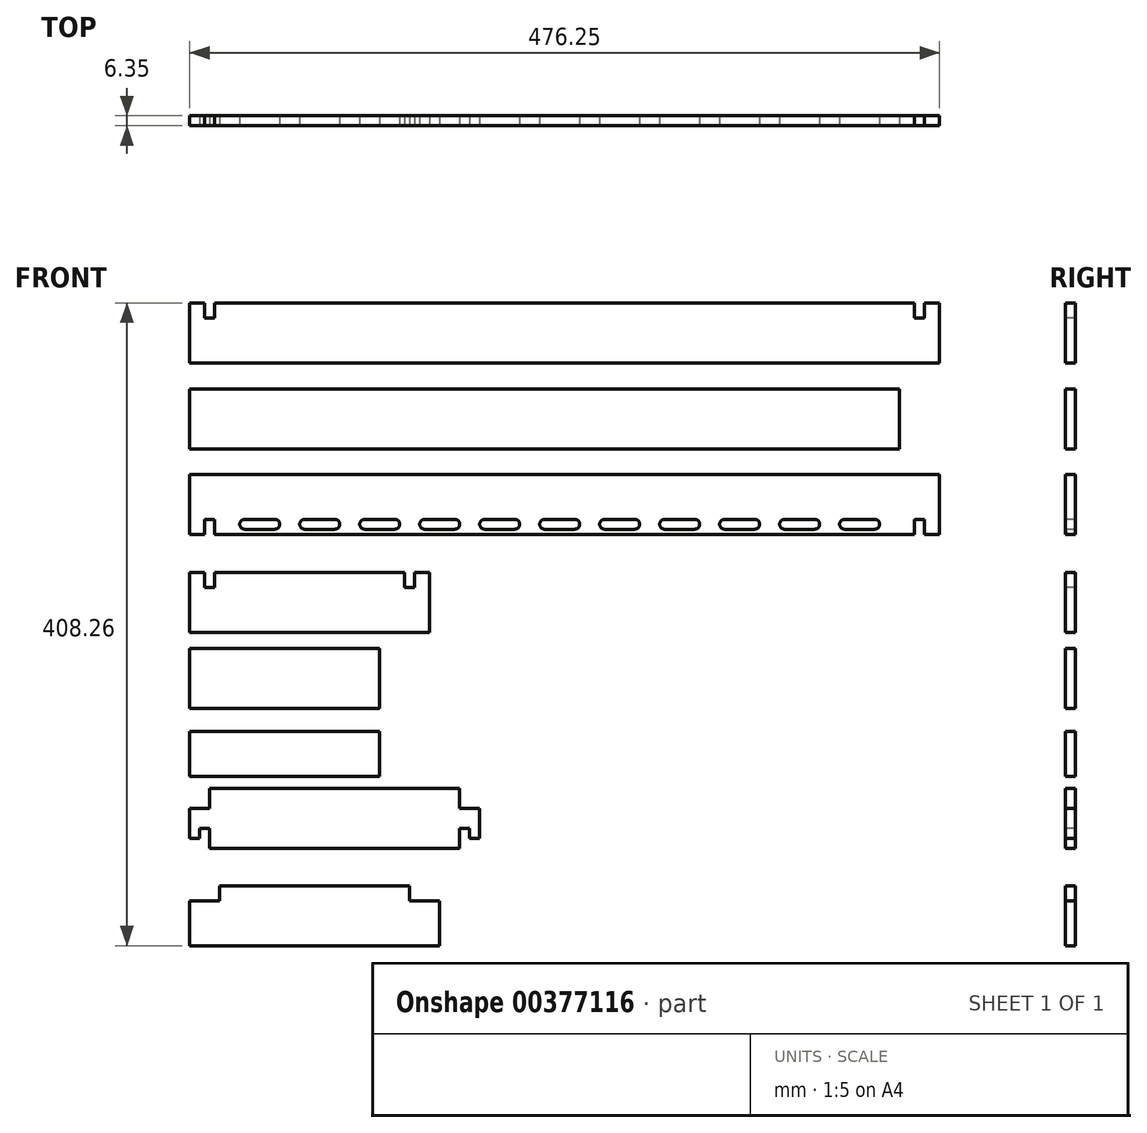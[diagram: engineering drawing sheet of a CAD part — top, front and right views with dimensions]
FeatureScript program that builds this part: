
annotation { "Feature Type Name" : "Feature", "Feature Type Description" : "" }
export const myFeature = defineFeature(function(context is Context, id is Id, definition is map)
    precondition{}
    {
        {
            var Q0;
            Q0=qCreatedBy(makeId("Front.planeOp"),FACE);
            var sketch = newSketch(context, id + "F0", { "sketchPlane" : qUnion([Q0])});
            skLineSegment(sketch, "E0.bottom", {"start": v(0, 0) * mm, "end": v(476.25, 0) * mm});
            skLineSegment(sketch, "E0.top", {"start": v(0, 38.1) * mm, "end": v(476.25, 38.1) * mm});
            skLineSegment(sketch, "E0.left", {"start": v(0, 0) * mm, "end": v(0, 38.1) * mm});
            skLineSegment(sketch, "E0.right", {"start": v(476.25, 0) * mm, "end": v(476.25, 38.1) * mm});
            skSolve(sketch);
        }
        {
            var Q0;
            Q0=qCreatedBy(makeId("Front.planeOp"),FACE);
            var sketch = newSketch(context, id + "F1", { "sketchPlane" : qUnion([Q0])});
            skLineSegment(sketch, "E1.bottom", {"start": v(0, -133.14) * mm, "end": v(152.4, -133.14) * mm});
            skLineSegment(sketch, "E1.top", {"start": v(0, -171.24) * mm, "end": v(152.4, -171.24) * mm});
            skLineSegment(sketch, "E1.left", {"start": v(0, -133.14) * mm, "end": v(0, -171.24) * mm});
            skLineSegment(sketch, "E1.right", {"start": v(152.4, -133.14) * mm, "end": v(152.4, -171.24) * mm});
            skLineSegment(sketch, "E2.bottom", {"start": v(0, -181.45) * mm, "end": v(120.65, -181.45) * mm});
            skLineSegment(sketch, "E2.top", {"start": v(0, -219.55) * mm, "end": v(120.65, -219.55) * mm});
            skLineSegment(sketch, "E2.left", {"start": v(0, -181.45) * mm, "end": v(0, -219.55) * mm});
            skLineSegment(sketch, "E2.right", {"start": v(120.65, -181.45) * mm, "end": v(120.65, -219.55) * mm});
            skLineSegment(sketch, "E3.bottom", {"start": v(0, -234.04) * mm, "end": v(120.65, -234.04) * mm});
            skLineSegment(sketch, "E3.top", {"start": v(0, -262.61) * mm, "end": v(120.65, -262.61) * mm});
            skLineSegment(sketch, "E3.left", {"start": v(0, -234.04) * mm, "end": v(0, -262.61) * mm});
            skLineSegment(sketch, "E3.right", {"start": v(120.65, -234.04) * mm, "end": v(120.65, -262.61) * mm});
            skLineSegment(sketch, "E4.bottom", {"start": v(0, -270.37) * mm, "end": v(184.15, -270.37) * mm});
            skLineSegment(sketch, "E4.top", {"start": v(0, -308.47) * mm, "end": v(184.15, -308.47) * mm});
            skLineSegment(sketch, "E4.left", {"start": v(0, -270.37) * mm, "end": v(0, -308.47) * mm});
            skLineSegment(sketch, "E4.right", {"start": v(184.15, -270.37) * mm, "end": v(184.15, -308.47) * mm});
            skLineSegment(sketch, "E5.bottom", {"start": v(0, -332.06) * mm, "end": v(158.75, -332.06) * mm});
            skLineSegment(sketch, "E5.top", {"start": v(0, -370.16) * mm, "end": v(158.75, -370.16) * mm});
            skLineSegment(sketch, "E5.left", {"start": v(0, -332.06) * mm, "end": v(0, -370.16) * mm});
            skLineSegment(sketch, "E5.right", {"start": v(158.75, -332.06) * mm, "end": v(158.75, -370.16) * mm});
            skSolve(sketch);
        }
        {
            var Q0;
            Q0=makeQuery(id+"F0.imprint","IMPRINT",FACE,{"disambiguationData":[TD([[makeQuery(id+"F0.imprint","IMPRINT",EDGE,{"derivedFrom":sQuery(id+"F0.wireOp",EDGE,"E0.bottom")}),1.0]])]});
            var Q1;
            Q1=makeQuery(id+"F1.imprint","IMPRINT",FACE,{"disambiguationData":[TD([[makeQuery(id+"F1.imprint","IMPRINT",EDGE,{"derivedFrom":sQuery(id+"F1.wireOp",EDGE,"E1.bottom")}),-1.0]])]});
            var Q2;
            Q2=makeQuery(id+"F1.imprint","IMPRINT",FACE,{"disambiguationData":[TD([[makeQuery(id+"F1.imprint","IMPRINT",EDGE,{"derivedFrom":sQuery(id+"F1.wireOp",EDGE,"E2.bottom")}),-1.0]])]});
            var Q3;
            Q3=makeQuery(id+"F1.imprint","IMPRINT",FACE,{"disambiguationData":[TD([[makeQuery(id+"F1.imprint","IMPRINT",EDGE,{"derivedFrom":sQuery(id+"F1.wireOp",EDGE,"E3.bottom")}),-1.0]])]});
            var Q4;
            Q4=makeQuery(id+"F1.imprint","IMPRINT",FACE,{"disambiguationData":[TD([[makeQuery(id+"F1.imprint","IMPRINT",EDGE,{"derivedFrom":sQuery(id+"F1.wireOp",EDGE,"E4.bottom")}),-1.0]])]});
            var Q5;
            Q5=makeQuery(id+"F1.imprint","IMPRINT",FACE,{"disambiguationData":[TD([[makeQuery(id+"F1.imprint","IMPRINT",EDGE,{"derivedFrom":sQuery(id+"F1.wireOp",EDGE,"E5.bottom")}),-1.0]])]});
            extrude(context, id + "F2", {"entities" : qUnion([Q0, Q1, Q2, Q3, Q4, Q5]), "oppositeDirection" : true, "depth" : 6.35 * mm});
        }
        {
            var Q0;
            Q0=qCreatedBy(makeId("Front.planeOp"),FACE);
            var sketch = newSketch(context, id + "F3", { "sketchPlane" : qUnion([Q0])});
            skLineSegment(sketch, "E6.bottom", {"start": v(0, -70.73) * mm, "end": v(476.25, -70.73) * mm});
            skLineSegment(sketch, "E6.top", {"start": v(0, -108.83) * mm, "end": v(476.25, -108.83) * mm});
            skLineSegment(sketch, "E6.left", {"start": v(0, -70.73) * mm, "end": v(0, -108.83) * mm});
            skLineSegment(sketch, "E6.right", {"start": v(476.25, -70.73) * mm, "end": v(476.25, -108.83) * mm});
            skSolve(sketch);
        }
        {
            var Q0;
            Q0 = qSketchRegion(id + "F3", true);
            extrude(context, id + "F4", {"entities" : qUnion([Q0]), "oppositeDirection" : true, "depth" : 6.35 * mm});
        }
        {
            var Q0;
            Q0=qCreatedBy(makeId("Front.planeOp"),FACE);
            var sketch = newSketch(context, id + "F5", { "sketchPlane" : qUnion([Q0])});
            skLineSegment(sketch, "E7.bottom", {"start": v(9.52, 38.1) * mm, "end": v(15.88, 38.1) * mm});
            skLineSegment(sketch, "E7.top", {"start": v(9.53, 28.58) * mm, "end": v(15.87, 28.58) * mm});
            skLineSegment(sketch, "E7.left", {"start": v(9.52, 38.1) * mm, "end": v(9.53, 28.58) * mm});
            skLineSegment(sketch, "E7.right", {"start": v(15.88, 38.1) * mm, "end": v(15.88, 28.58) * mm});
            skLineSegment(sketch, "E8.bottom", {"start": v(460.38, 38.1) * mm, "end": v(466.73, 38.1) * mm});
            skLineSegment(sketch, "E8.top", {"start": v(460.38, 28.58) * mm, "end": v(466.73, 28.58) * mm});
            skLineSegment(sketch, "E8.left", {"start": v(460.38, 38.1) * mm, "end": v(460.38, 28.58) * mm});
            skLineSegment(sketch, "E8.right", {"start": v(466.73, 38.1) * mm, "end": v(466.73, 28.58) * mm});
            skLineSegment(sketch, "E9.bottom", {"start": v(9.53, -108.83) * mm, "end": v(15.87, -108.83) * mm});
            skLineSegment(sketch, "E9.top", {"start": v(9.52, -99.3) * mm, "end": v(15.87, -99.3) * mm});
            skLineSegment(sketch, "E9.left", {"start": v(9.53, -108.83) * mm, "end": v(9.52, -99.3) * mm});
            skLineSegment(sketch, "E9.right", {"start": v(15.87, -108.83) * mm, "end": v(15.87, -99.3) * mm});
            skLineSegment(sketch, "E10.bottom", {"start": v(460.38, -99.3) * mm, "end": v(466.73, -99.3) * mm});
            skLineSegment(sketch, "E10.top", {"start": v(460.38, -108.83) * mm, "end": v(466.73, -108.83) * mm});
            skLineSegment(sketch, "E10.left", {"start": v(460.38, -99.3) * mm, "end": v(460.38, -108.83) * mm});
            skLineSegment(sketch, "E10.right", {"start": v(466.73, -99.3) * mm, "end": v(466.73, -108.83) * mm});
            skLineSegment(sketch, "E11.bottom", {"start": v(9.53, -133.14) * mm, "end": v(15.87, -133.14) * mm});
            skLineSegment(sketch, "E11.top", {"start": v(9.53, -142.66) * mm, "end": v(15.87, -142.66) * mm});
            skLineSegment(sketch, "E11.left", {"start": v(9.53, -133.14) * mm, "end": v(9.53, -142.66) * mm});
            skLineSegment(sketch, "E11.right", {"start": v(15.87, -133.14) * mm, "end": v(15.87, -142.66) * mm});
            skLineSegment(sketch, "E12.bottom", {"start": v(136.53, -142.66) * mm, "end": v(142.88, -142.66) * mm});
            skLineSegment(sketch, "E12.top", {"start": v(136.53, -133.14) * mm, "end": v(142.88, -133.14) * mm});
            skLineSegment(sketch, "E12.left", {"start": v(136.53, -142.66) * mm, "end": v(136.53, -133.14) * mm});
            skLineSegment(sketch, "E12.right", {"start": v(142.88, -142.66) * mm, "end": v(142.88, -133.14) * mm});
            skLineSegment(sketch, "E13.bottom", {"start": v(34.93, -99.3) * mm, "end": v(53.98, -99.3) * mm});
            skLineSegment(sketch, "E13.top", {"start": v(34.93, -105.66) * mm, "end": v(53.98, -105.66) * mm});
            skLineSegment(sketch, "E13.left", {"start": v(31.75, -102.48) * mm, "end": v(31.75, -102.48) * mm});
            skLineSegment(sketch, "E13.right", {"start": v(57.15, -102.48) * mm, "end": v(57.15, -102.48) * mm});
            skPoint(sketch, "E14.visualSharp", {"position": v(31.75, -99.3) * mm});
            skArc(sketch, "E14.filletArc", {"start": v(34.93, -99.3) * mm, "mid": v(32.68, -100.24) * mm, "end": v(31.75, -102.48) * mm});
            skPoint(sketch, "E15.visualSharp", {"position": v(31.75, -105.66) * mm});
            skArc(sketch, "E15.filletArc", {"start": v(31.75, -102.48) * mm, "mid": v(32.68, -104.73) * mm, "end": v(34.93, -105.66) * mm});
            skPoint(sketch, "E16.visualSharp", {"position": v(57.15, -105.66) * mm});
            skArc(sketch, "E16.filletArc", {"start": v(53.98, -105.66) * mm, "mid": v(56.22, -104.73) * mm, "end": v(57.15, -102.48) * mm});
            skPoint(sketch, "E17.visualSharp", {"position": v(57.15, -99.3) * mm});
            skArc(sketch, "E17.filletArc", {"start": v(57.15, -102.48) * mm, "mid": v(56.22, -100.24) * mm, "end": v(53.98, -99.3) * mm});
            skArc(sketch, "E18.1.0.0", {"start": v(73.02, -99.3) * mm, "mid": v(70.78, -100.24) * mm, "end": v(69.85, -102.48) * mm});
            skArc(sketch, "E18.1.0.1", {"start": v(69.85, -102.48) * mm, "mid": v(70.78, -104.73) * mm, "end": v(73.02, -105.66) * mm});
            skLineSegment(sketch, "E18.1.0.2", {"start": v(73.02, -105.66) * mm, "end": v(92.07, -105.66) * mm});
            skArc(sketch, "E18.1.0.3", {"start": v(92.07, -105.66) * mm, "mid": v(94.32, -104.73) * mm, "end": v(95.25, -102.48) * mm});
            skArc(sketch, "E18.1.0.4", {"start": v(95.25, -102.48) * mm, "mid": v(94.32, -100.24) * mm, "end": v(92.07, -99.3) * mm});
            skLineSegment(sketch, "E18.1.0.5", {"start": v(73.02, -99.3) * mm, "end": v(92.07, -99.3) * mm});
            skArc(sketch, "E18.2.0.0", {"start": v(111.12, -99.3) * mm, "mid": v(108.88, -100.24) * mm, "end": v(107.95, -102.48) * mm});
            skArc(sketch, "E18.2.0.1", {"start": v(107.95, -102.48) * mm, "mid": v(108.88, -104.73) * mm, "end": v(111.12, -105.66) * mm});
            skLineSegment(sketch, "E18.2.0.2", {"start": v(111.12, -105.66) * mm, "end": v(130.17, -105.66) * mm});
            skArc(sketch, "E18.2.0.3", {"start": v(130.17, -105.66) * mm, "mid": v(132.42, -104.73) * mm, "end": v(133.35, -102.48) * mm});
            skArc(sketch, "E18.2.0.4", {"start": v(133.35, -102.48) * mm, "mid": v(132.42, -100.24) * mm, "end": v(130.17, -99.3) * mm});
            skLineSegment(sketch, "E18.2.0.5", {"start": v(111.12, -99.3) * mm, "end": v(130.17, -99.3) * mm});
            skLineSegment(sketch, "E18.direction1", {"start": v(31.75, -102.48) * mm, "end": v(69.85, -102.48) * mm, "construction": true});
            skArc(sketch, "E19.0.3.0", {"start": v(149.22, -99.3) * mm, "mid": v(146.98, -100.24) * mm, "end": v(146.05, -102.48) * mm});
            skArc(sketch, "E19.4.3.0", {"start": v(146.05, -102.48) * mm, "mid": v(146.98, -104.73) * mm, "end": v(149.22, -105.66) * mm});
            skLineSegment(sketch, "E19.8.3.0", {"start": v(149.22, -105.66) * mm, "end": v(168.27, -105.66) * mm});
            skArc(sketch, "E19.11.3.0", {"start": v(168.27, -105.66) * mm, "mid": v(170.52, -104.73) * mm, "end": v(171.45, -102.48) * mm});
            skArc(sketch, "E19.15.3.0", {"start": v(171.45, -102.48) * mm, "mid": v(170.52, -100.24) * mm, "end": v(168.27, -99.3) * mm});
            skLineSegment(sketch, "E19.19.3.0", {"start": v(149.22, -99.3) * mm, "end": v(168.27, -99.3) * mm});
            skArc(sketch, "E19.0.4.0", {"start": v(187.32, -99.3) * mm, "mid": v(185.08, -100.24) * mm, "end": v(184.15, -102.48) * mm});
            skArc(sketch, "E19.4.4.0", {"start": v(184.15, -102.48) * mm, "mid": v(185.08, -104.73) * mm, "end": v(187.32, -105.66) * mm});
            skLineSegment(sketch, "E19.8.4.0", {"start": v(187.32, -105.66) * mm, "end": v(206.37, -105.66) * mm});
            skArc(sketch, "E19.11.4.0", {"start": v(206.37, -105.66) * mm, "mid": v(208.62, -104.73) * mm, "end": v(209.55, -102.48) * mm});
            skArc(sketch, "E19.15.4.0", {"start": v(209.55, -102.48) * mm, "mid": v(208.62, -100.24) * mm, "end": v(206.37, -99.3) * mm});
            skLineSegment(sketch, "E19.19.4.0", {"start": v(187.32, -99.3) * mm, "end": v(206.37, -99.3) * mm});
            skArc(sketch, "E20.0.5.0", {"start": v(225.42, -99.3) * mm, "mid": v(223.18, -100.24) * mm, "end": v(222.25, -102.48) * mm});
            skArc(sketch, "E20.4.5.0", {"start": v(222.25, -102.48) * mm, "mid": v(223.18, -104.73) * mm, "end": v(225.42, -105.66) * mm});
            skLineSegment(sketch, "E20.8.5.0", {"start": v(225.42, -105.66) * mm, "end": v(244.47, -105.66) * mm});
            skArc(sketch, "E20.11.5.0", {"start": v(244.47, -105.66) * mm, "mid": v(246.72, -104.73) * mm, "end": v(247.65, -102.48) * mm});
            skArc(sketch, "E20.15.5.0", {"start": v(247.65, -102.48) * mm, "mid": v(246.72, -100.24) * mm, "end": v(244.47, -99.3) * mm});
            skLineSegment(sketch, "E20.19.5.0", {"start": v(225.42, -99.3) * mm, "end": v(244.47, -99.3) * mm});
            skArc(sketch, "E20.0.6.0", {"start": v(263.52, -99.3) * mm, "mid": v(261.28, -100.24) * mm, "end": v(260.35, -102.48) * mm});
            skArc(sketch, "E20.4.6.0", {"start": v(260.35, -102.48) * mm, "mid": v(261.28, -104.73) * mm, "end": v(263.52, -105.66) * mm});
            skLineSegment(sketch, "E20.8.6.0", {"start": v(263.52, -105.66) * mm, "end": v(282.57, -105.66) * mm});
            skArc(sketch, "E20.11.6.0", {"start": v(282.57, -105.66) * mm, "mid": v(284.82, -104.73) * mm, "end": v(285.75, -102.48) * mm});
            skArc(sketch, "E20.15.6.0", {"start": v(285.75, -102.48) * mm, "mid": v(284.82, -100.24) * mm, "end": v(282.57, -99.3) * mm});
            skLineSegment(sketch, "E20.19.6.0", {"start": v(263.52, -99.3) * mm, "end": v(282.57, -99.3) * mm});
            skArc(sketch, "E20.0.7.0", {"start": v(301.62, -99.3) * mm, "mid": v(299.38, -100.24) * mm, "end": v(298.45, -102.48) * mm});
            skArc(sketch, "E20.4.7.0", {"start": v(298.45, -102.48) * mm, "mid": v(299.38, -104.73) * mm, "end": v(301.62, -105.66) * mm});
            skLineSegment(sketch, "E20.8.7.0", {"start": v(301.62, -105.66) * mm, "end": v(320.67, -105.66) * mm});
            skArc(sketch, "E20.11.7.0", {"start": v(320.67, -105.66) * mm, "mid": v(322.92, -104.73) * mm, "end": v(323.85, -102.48) * mm});
            skArc(sketch, "E20.15.7.0", {"start": v(323.85, -102.48) * mm, "mid": v(322.92, -100.24) * mm, "end": v(320.67, -99.3) * mm});
            skLineSegment(sketch, "E20.19.7.0", {"start": v(301.62, -99.3) * mm, "end": v(320.67, -99.3) * mm});
            skArc(sketch, "E20.0.8.0", {"start": v(339.72, -99.3) * mm, "mid": v(337.48, -100.24) * mm, "end": v(336.55, -102.48) * mm});
            skArc(sketch, "E20.4.8.0", {"start": v(336.55, -102.48) * mm, "mid": v(337.48, -104.73) * mm, "end": v(339.72, -105.66) * mm});
            skLineSegment(sketch, "E20.8.8.0", {"start": v(339.72, -105.66) * mm, "end": v(358.77, -105.66) * mm});
            skArc(sketch, "E20.11.8.0", {"start": v(358.77, -105.66) * mm, "mid": v(361.02, -104.73) * mm, "end": v(361.95, -102.48) * mm});
            skArc(sketch, "E20.15.8.0", {"start": v(361.95, -102.48) * mm, "mid": v(361.02, -100.24) * mm, "end": v(358.77, -99.3) * mm});
            skLineSegment(sketch, "E20.19.8.0", {"start": v(339.72, -99.3) * mm, "end": v(358.77, -99.3) * mm});
            skArc(sketch, "E20.0.9.0", {"start": v(377.82, -99.3) * mm, "mid": v(375.58, -100.24) * mm, "end": v(374.65, -102.48) * mm});
            skArc(sketch, "E20.4.9.0", {"start": v(374.65, -102.48) * mm, "mid": v(375.58, -104.73) * mm, "end": v(377.82, -105.66) * mm});
            skLineSegment(sketch, "E20.8.9.0", {"start": v(377.82, -105.66) * mm, "end": v(396.87, -105.66) * mm});
            skArc(sketch, "E20.11.9.0", {"start": v(396.87, -105.66) * mm, "mid": v(399.12, -104.73) * mm, "end": v(400.05, -102.48) * mm});
            skArc(sketch, "E20.15.9.0", {"start": v(400.05, -102.48) * mm, "mid": v(399.12, -100.24) * mm, "end": v(396.87, -99.3) * mm});
            skLineSegment(sketch, "E20.19.9.0", {"start": v(377.82, -99.3) * mm, "end": v(396.87, -99.3) * mm});
            skLineSegment(sketch, "E21.bottom", {"start": v(0, -270.37) * mm, "end": v(12.7, -270.37) * mm});
            skLineSegment(sketch, "E21.top", {"start": v(0, -283.07) * mm, "end": v(12.7, -283.07) * mm});
            skLineSegment(sketch, "E21.left", {"start": v(0, -270.37) * mm, "end": v(0, -283.07) * mm});
            skLineSegment(sketch, "E21.right", {"start": v(12.7, -270.37) * mm, "end": v(12.7, -283.07) * mm});
            skLineSegment(sketch, "E22.bottom", {"start": v(184.15, -270.37) * mm, "end": v(171.45, -270.37) * mm});
            skLineSegment(sketch, "E22.top", {"start": v(184.15, -283.07) * mm, "end": v(171.45, -283.07) * mm});
            skLineSegment(sketch, "E22.left", {"start": v(184.15, -270.37) * mm, "end": v(184.15, -283.07) * mm});
            skLineSegment(sketch, "E22.right", {"start": v(171.45, -270.37) * mm, "end": v(171.45, -283.07) * mm});
            skLineSegment(sketch, "E23.bottom", {"start": v(171.45, -295.77) * mm, "end": v(177.8, -295.77) * mm});
            skLineSegment(sketch, "E23.left", {"start": v(171.45, -295.77) * mm, "end": v(171.45, -308.47) * mm});
            skLineSegment(sketch, "E24.bottom", {"start": v(6.35, -295.77) * mm, "end": v(12.7, -295.77) * mm});
            skLineSegment(sketch, "E24.top", {"start": v(0, -308.47) * mm, "end": v(12.7, -308.47) * mm});
            skLineSegment(sketch, "E24.right", {"start": v(12.7, -295.77) * mm, "end": v(12.7, -308.47) * mm});
            skLineSegment(sketch, "E25", {"start": v(0, -308.47) * mm, "end": v(0, -302.12) * mm});
            skLineSegment(sketch, "E26", {"start": v(0, -302.12) * mm, "end": v(6.35, -302.12) * mm});
            skLineSegment(sketch, "E27", {"start": v(6.35, -302.12) * mm, "end": v(6.35, -295.77) * mm});
            skLineSegment(sketch, "E28", {"start": v(177.8, -295.77) * mm, "end": v(177.8, -302.12) * mm});
            skLineSegment(sketch, "E29", {"start": v(177.8, -302.12) * mm, "end": v(184.15, -302.12) * mm});
            skLineSegment(sketch, "E30", {"start": v(184.15, -302.12) * mm, "end": v(184.15, -308.47) * mm});
            skLineSegment(sketch, "E31", {"start": v(171.45, -308.47) * mm, "end": v(184.15, -308.47) * mm});
            skLineSegment(sketch, "E32.bottom", {"start": v(0, -332.06) * mm, "end": v(19.05, -332.06) * mm});
            skLineSegment(sketch, "E32.top", {"start": v(0, -341.59) * mm, "end": v(19.05, -341.59) * mm});
            skLineSegment(sketch, "E32.left", {"start": v(0, -332.06) * mm, "end": v(0, -341.59) * mm});
            skLineSegment(sketch, "E32.right", {"start": v(19.05, -332.06) * mm, "end": v(19.05, -341.59) * mm});
            skLineSegment(sketch, "E33.bottom", {"start": v(139.7, -332.06) * mm, "end": v(158.75, -332.06) * mm});
            skLineSegment(sketch, "E33.top", {"start": v(139.7, -341.59) * mm, "end": v(158.75, -341.59) * mm});
            skLineSegment(sketch, "E33.left", {"start": v(139.7, -332.06) * mm, "end": v(139.7, -341.59) * mm});
            skLineSegment(sketch, "E33.right", {"start": v(158.75, -332.06) * mm, "end": v(158.75, -341.59) * mm});
            skArc(sketch, "E34.0.10.0", {"start": v(415.92, -99.3) * mm, "mid": v(413.68, -100.24) * mm, "end": v(412.75, -102.48) * mm});
            skArc(sketch, "E34.4.10.0", {"start": v(412.75, -102.48) * mm, "mid": v(413.68, -104.73) * mm, "end": v(415.92, -105.66) * mm});
            skLineSegment(sketch, "E34.8.10.0", {"start": v(415.92, -105.66) * mm, "end": v(434.97, -105.66) * mm});
            skArc(sketch, "E34.11.10.0", {"start": v(434.97, -105.66) * mm, "mid": v(437.22, -104.73) * mm, "end": v(438.15, -102.48) * mm});
            skArc(sketch, "E34.15.10.0", {"start": v(438.15, -102.48) * mm, "mid": v(437.22, -100.24) * mm, "end": v(434.97, -99.3) * mm});
            skLineSegment(sketch, "E34.19.10.0", {"start": v(415.92, -99.3) * mm, "end": v(434.97, -99.3) * mm});
            skSolve(sketch);
        }
        {
            var Q0;
            Q0 = qSketchRegion(id + "F5", true);
            extrude(context, id + "F6", {"entities" : qUnion([Q0]), "operationType" : NewBodyOperationType.REMOVE, "endBound" : BoundingType.UP_TO_NEXT, "oppositeDirection" : true, "depth" : 25.4 * mm});
        }
        {
            var Q0;
            {var subQ0=sQuery(id+"F1.wireOp",EDGE,"E1.bottom");Q0=makeQuery(id+"F6.boolean.opBoolean","SPLIT",EDGE,{"disambiguationData":[TD([makeQuery(id+"F6.opExtrude","SWEPT_FACE",FACE,{"disambiguationData":[OSD([sQuery(id+"F5.wireOp",EDGE,"E11.right")])]})])],"derivedFrom":makeQuery(id+"F2.opExtrude","CAP_EDGE",EDGE,{"disambiguationData":[OSD([subQ0])],"isStart":false})});}
            var Q1;
            {var subQ0=sQuery(id+"F0.wireOp",EDGE,"E0.top");Q1=makeQuery(id+"F6.boolean.opBoolean","SPLIT",EDGE,{"disambiguationData":[TD([makeQuery(id+"F6.opExtrude","SWEPT_FACE",FACE,{"disambiguationData":[OSD([sQuery(id+"F5.wireOp",EDGE,"E7.right")])]})])],"derivedFrom":makeQuery(id+"F2.opExtrude","CAP_EDGE",EDGE,{"disambiguationData":[OSD([subQ0])],"isStart":true})});}
            var Q2;
            {var subQ0=sQuery(id+"F0.wireOp",EDGE,"E0.top");Q2=makeQuery(id+"F6.boolean.opBoolean","SPLIT",EDGE,{"disambiguationData":[TD([makeQuery(id+"F6.opExtrude","SWEPT_FACE",FACE,{"disambiguationData":[OSD([sQuery(id+"F5.wireOp",EDGE,"E7.right")])]})])],"derivedFrom":makeQuery(id+"F2.opExtrude","CAP_EDGE",EDGE,{"disambiguationData":[OSD([subQ0])],"isStart":false})});}
            var Q3;
            {var subQ0=sQuery(id+"F3.wireOp",EDGE,"E6.top");Q3=makeQuery(id+"F6.boolean.opBoolean","SPLIT",EDGE,{"disambiguationData":[TD([makeQuery(id+"F6.opExtrude","SWEPT_FACE",FACE,{"disambiguationData":[OSD([sQuery(id+"F5.wireOp",EDGE,"E9.right")])]})])],"derivedFrom":makeQuery(id+"F4.opExtrude","CAP_EDGE",EDGE,{"disambiguationData":[OSD([subQ0])],"isStart":true})});}
            var Q4;
            {var subQ0=sQuery(id+"F3.wireOp",EDGE,"E6.top");Q4=makeQuery(id+"F6.boolean.opBoolean","SPLIT",EDGE,{"disambiguationData":[TD([makeQuery(id+"F6.opExtrude","SWEPT_FACE",FACE,{"disambiguationData":[OSD([sQuery(id+"F5.wireOp",EDGE,"E9.right")])]})])],"derivedFrom":makeQuery(id+"F4.opExtrude","CAP_EDGE",EDGE,{"disambiguationData":[OSD([subQ0])],"isStart":false})});}
            var Q5;
            Q5=makeQuery(id+"F6.boolean.opBoolean","COPY",EDGE,{"derivedFrom":makeQuery(id+"F6.opExtrude","TWEAK_EDGE",EDGE,{"derivedFrom":[makeQuery(id+"F4.opExtrude","CAP_FACE",FACE,{"disambiguationData":[OSD([sQuery(id+"F3.wireOp",EDGE,"E6.bottom"),sQuery(id+"F3.wireOp",EDGE,"E6.top"),sQuery(id+"F3.wireOp",EDGE,"E6.left"),sQuery(id+"F3.wireOp",EDGE,"E6.right")])],"isStart":false}),makeQuery(id+"F5.imprint","IMPRINT",EDGE,{"derivedFrom":sQuery(id+"F5.wireOp",EDGE,"E9.top")})]})});
            var Q6;
            Q6=makeQuery(id+"F6.boolean.opBoolean","COPY",EDGE,{"derivedFrom":makeQuery(id+"F6.opExtrude","CAP_EDGE",EDGE,{"disambiguationData":[OSD([sQuery(id+"F5.wireOp",EDGE,"E9.top")])],"isStart":true})});
            var Q7;
            Q7=makeQuery(id+"F6.boolean.opBoolean","COPY",EDGE,{"derivedFrom":makeQuery(id+"F6.opExtrude","CAP_EDGE",EDGE,{"disambiguationData":[OSD([sQuery(id+"F5.wireOp",EDGE,"E10.bottom")])],"isStart":true})});
            var Q8;
            Q8=makeQuery(id+"F6.boolean.opBoolean","COPY",EDGE,{"derivedFrom":makeQuery(id+"F6.opExtrude","TWEAK_EDGE",EDGE,{"derivedFrom":[makeQuery(id+"F4.opExtrude","CAP_FACE",FACE,{"disambiguationData":[OSD([sQuery(id+"F3.wireOp",EDGE,"E6.bottom"),sQuery(id+"F3.wireOp",EDGE,"E6.top"),sQuery(id+"F3.wireOp",EDGE,"E6.left"),sQuery(id+"F3.wireOp",EDGE,"E6.right")])],"isStart":false}),makeQuery(id+"F5.imprint","IMPRINT",EDGE,{"derivedFrom":sQuery(id+"F5.wireOp",EDGE,"E10.bottom")})]})});
            var Q9;
            {var subQ0=sQuery(id+"F1.wireOp",EDGE,"E1.bottom");Q9=makeQuery(id+"F6.boolean.opBoolean","SPLIT",EDGE,{"disambiguationData":[TD([makeQuery(id+"F6.opExtrude","SWEPT_FACE",FACE,{"disambiguationData":[OSD([sQuery(id+"F5.wireOp",EDGE,"E11.right")])]})])],"derivedFrom":makeQuery(id+"F2.opExtrude","CAP_EDGE",EDGE,{"disambiguationData":[OSD([subQ0])],"isStart":true})});}
            var Q10;
            Q10=makeQuery(id+"F6.boolean.opBoolean","COPY",EDGE,{"derivedFrom":makeQuery(id+"F6.opExtrude","TWEAK_EDGE",EDGE,{"derivedFrom":[makeQuery(id+"F2.opExtrude","CAP_FACE",FACE,{"disambiguationData":[OSD([sQuery(id+"F1.wireOp",EDGE,"E1.bottom"),sQuery(id+"F1.wireOp",EDGE,"E1.top"),sQuery(id+"F1.wireOp",EDGE,"E1.left"),sQuery(id+"F1.wireOp",EDGE,"E1.right")])],"isStart":false}),makeQuery(id+"F5.imprint","IMPRINT",EDGE,{"derivedFrom":sQuery(id+"F5.wireOp",EDGE,"E11.top")})]})});
            var Q11;
            Q11=makeQuery(id+"F6.boolean.opBoolean","COPY",EDGE,{"derivedFrom":makeQuery(id+"F6.opExtrude","CAP_EDGE",EDGE,{"disambiguationData":[OSD([sQuery(id+"F5.wireOp",EDGE,"E12.bottom")])],"isStart":true})});
            var Q12;
            Q12=makeQuery(id+"F6.boolean.opBoolean","COPY",EDGE,{"derivedFrom":makeQuery(id+"F6.opExtrude","TWEAK_EDGE",EDGE,{"derivedFrom":[makeQuery(id+"F2.opExtrude","CAP_FACE",FACE,{"disambiguationData":[OSD([sQuery(id+"F1.wireOp",EDGE,"E1.bottom"),sQuery(id+"F1.wireOp",EDGE,"E1.top"),sQuery(id+"F1.wireOp",EDGE,"E1.left"),sQuery(id+"F1.wireOp",EDGE,"E1.right")])],"isStart":false}),makeQuery(id+"F5.imprint","IMPRINT",EDGE,{"derivedFrom":sQuery(id+"F5.wireOp",EDGE,"E12.bottom")})]})});
            var Q13;
            Q13=makeQuery(id+"F6.boolean.opBoolean","COPY",EDGE,{"derivedFrom":makeQuery(id+"F6.opExtrude","CAP_EDGE",EDGE,{"disambiguationData":[OSD([sQuery(id+"F5.wireOp",EDGE,"E11.top")])],"isStart":true})});
            var Q14;
            Q14=makeQuery(id+"F6.boolean.opBoolean","COPY",EDGE,{"derivedFrom":makeQuery(id+"F6.opExtrude","CAP_EDGE",EDGE,{"disambiguationData":[OSD([sQuery(id+"F5.wireOp",EDGE,"E7.top")])],"isStart":true})});
            var Q15;
            Q15=makeQuery(id+"F6.boolean.opBoolean","COPY",EDGE,{"derivedFrom":makeQuery(id+"F6.opExtrude","TWEAK_EDGE",EDGE,{"derivedFrom":[makeQuery(id+"F2.opExtrude","CAP_FACE",FACE,{"disambiguationData":[OSD([sQuery(id+"F0.wireOp",EDGE,"E0.bottom"),sQuery(id+"F0.wireOp",EDGE,"E0.top"),sQuery(id+"F0.wireOp",EDGE,"E0.left"),sQuery(id+"F0.wireOp",EDGE,"E0.right")])],"isStart":false}),makeQuery(id+"F5.imprint","IMPRINT",EDGE,{"derivedFrom":sQuery(id+"F5.wireOp",EDGE,"E7.top")})]})});
            var Q16;
            Q16=makeQuery(id+"F6.boolean.opBoolean","COPY",EDGE,{"derivedFrom":makeQuery(id+"F6.opExtrude","TWEAK_EDGE",EDGE,{"derivedFrom":[makeQuery(id+"F2.opExtrude","CAP_FACE",FACE,{"disambiguationData":[OSD([sQuery(id+"F0.wireOp",EDGE,"E0.bottom"),sQuery(id+"F0.wireOp",EDGE,"E0.top"),sQuery(id+"F0.wireOp",EDGE,"E0.left"),sQuery(id+"F0.wireOp",EDGE,"E0.right")])],"isStart":false}),makeQuery(id+"F5.imprint","IMPRINT",EDGE,{"derivedFrom":sQuery(id+"F5.wireOp",EDGE,"E8.top")})]})});
            var Q17;
            Q17=makeQuery(id+"F6.boolean.opBoolean","COPY",EDGE,{"derivedFrom":makeQuery(id+"F6.opExtrude","CAP_EDGE",EDGE,{"disambiguationData":[OSD([sQuery(id+"F5.wireOp",EDGE,"E8.top")])],"isStart":true})});
            var Q18;
            Q18=makeQuery(id+"F6.boolean.opBoolean","COPY",EDGE,{"derivedFrom":makeQuery(id+"F6.opExtrude","CAP_EDGE",EDGE,{"disambiguationData":[OSD([sQuery(id+"F5.wireOp",EDGE,"BUo8Hppx-LPfE-Cc0y-CvPR-yRLmtIfKfLPI.bottom")])],"isStart":true})});
            var Q19;
            Q19=makeQuery(id+"F6.boolean.opBoolean","COPY",EDGE,{"derivedFrom":makeQuery(id+"F6.opExtrude","TWEAK_EDGE",EDGE,{"derivedFrom":[makeQuery(id+"F2.opExtrude","CAP_FACE",FACE,{"disambiguationData":[OSD([sQuery(id+"F1.wireOp",EDGE,"E3.bottom"),sQuery(id+"F1.wireOp",EDGE,"E3.top"),sQuery(id+"F1.wireOp",EDGE,"E3.left"),sQuery(id+"F1.wireOp",EDGE,"E3.right")])],"isStart":false}),makeQuery(id+"F5.imprint","IMPRINT",EDGE,{"derivedFrom":sQuery(id+"F5.wireOp",EDGE,"BUo8Hppx-LPfE-Cc0y-CvPR-yRLmtIfKfLPI.bottom")})]})});
            var Q20;
            Q20=makeQuery(id+"F6.boolean.opBoolean","COPY",EDGE,{"derivedFrom":makeQuery(id+"F6.opExtrude","CAP_EDGE",EDGE,{"disambiguationData":[OSD([sQuery(id+"F5.wireOp",EDGE,"OH6TwauT-DVMZ-jRhG-AgCz-VgdMOrD31Yf2.bottom")])],"isStart":true})});
            var Q21;
            Q21=makeQuery(id+"F6.boolean.opBoolean","COPY",EDGE,{"derivedFrom":makeQuery(id+"F6.opExtrude","TWEAK_EDGE",EDGE,{"derivedFrom":[makeQuery(id+"F2.opExtrude","CAP_FACE",FACE,{"disambiguationData":[OSD([sQuery(id+"F1.wireOp",EDGE,"E3.bottom"),sQuery(id+"F1.wireOp",EDGE,"E3.top"),sQuery(id+"F1.wireOp",EDGE,"E3.left"),sQuery(id+"F1.wireOp",EDGE,"E3.right")])],"isStart":false}),makeQuery(id+"F5.imprint","IMPRINT",EDGE,{"derivedFrom":sQuery(id+"F5.wireOp",EDGE,"OH6TwauT-DVMZ-jRhG-AgCz-VgdMOrD31Yf2.bottom")})]})});
            fillet(context, id + "F7", {"entities" : qUnion([Q0, Q1, Q2, Q3, Q4, Q5, Q6, Q7, Q8, Q9, Q10, Q11, Q12, Q13, Q14, Q15, Q16, Q17, Q18, Q19, Q20, Q21]), "radius" : 3.17 * mm, "tangentPropagation" : true, "allowEdgeOverflow" : false});
        }
        {
            var Q0;
            Q0=qCreatedBy(makeId("Front.planeOp"),FACE);
            var sketch = newSketch(context, id + "F8", { "sketchPlane" : qUnion([Q0])});
            skLineSegment(sketch, "E35.bottom", {"start": v(0, -16.72) * mm, "end": v(450.85, -16.72) * mm});
            skLineSegment(sketch, "E35.top", {"start": v(0, -54.82) * mm, "end": v(450.85, -54.82) * mm});
            skLineSegment(sketch, "E35.left", {"start": v(0, -16.72) * mm, "end": v(0, -54.82) * mm});
            skLineSegment(sketch, "E35.right", {"start": v(450.85, -16.72) * mm, "end": v(450.85, -54.82) * mm});
            skSolve(sketch);
        }
        {
            var Q0;
            Q0=makeQuery(id+"F8.imprint","IMPRINT",FACE,{"disambiguationData":[TD([[makeQuery(id+"F8.imprint","IMPRINT",EDGE,{"derivedFrom":sQuery(id+"F8.wireOp",EDGE,"E35.bottom")}),-1.0]])]});
            extrude(context, id + "F9", {"entities" : qUnion([Q0]), "oppositeDirection" : true, "depth" : 6.35 * mm});
        }
    });
